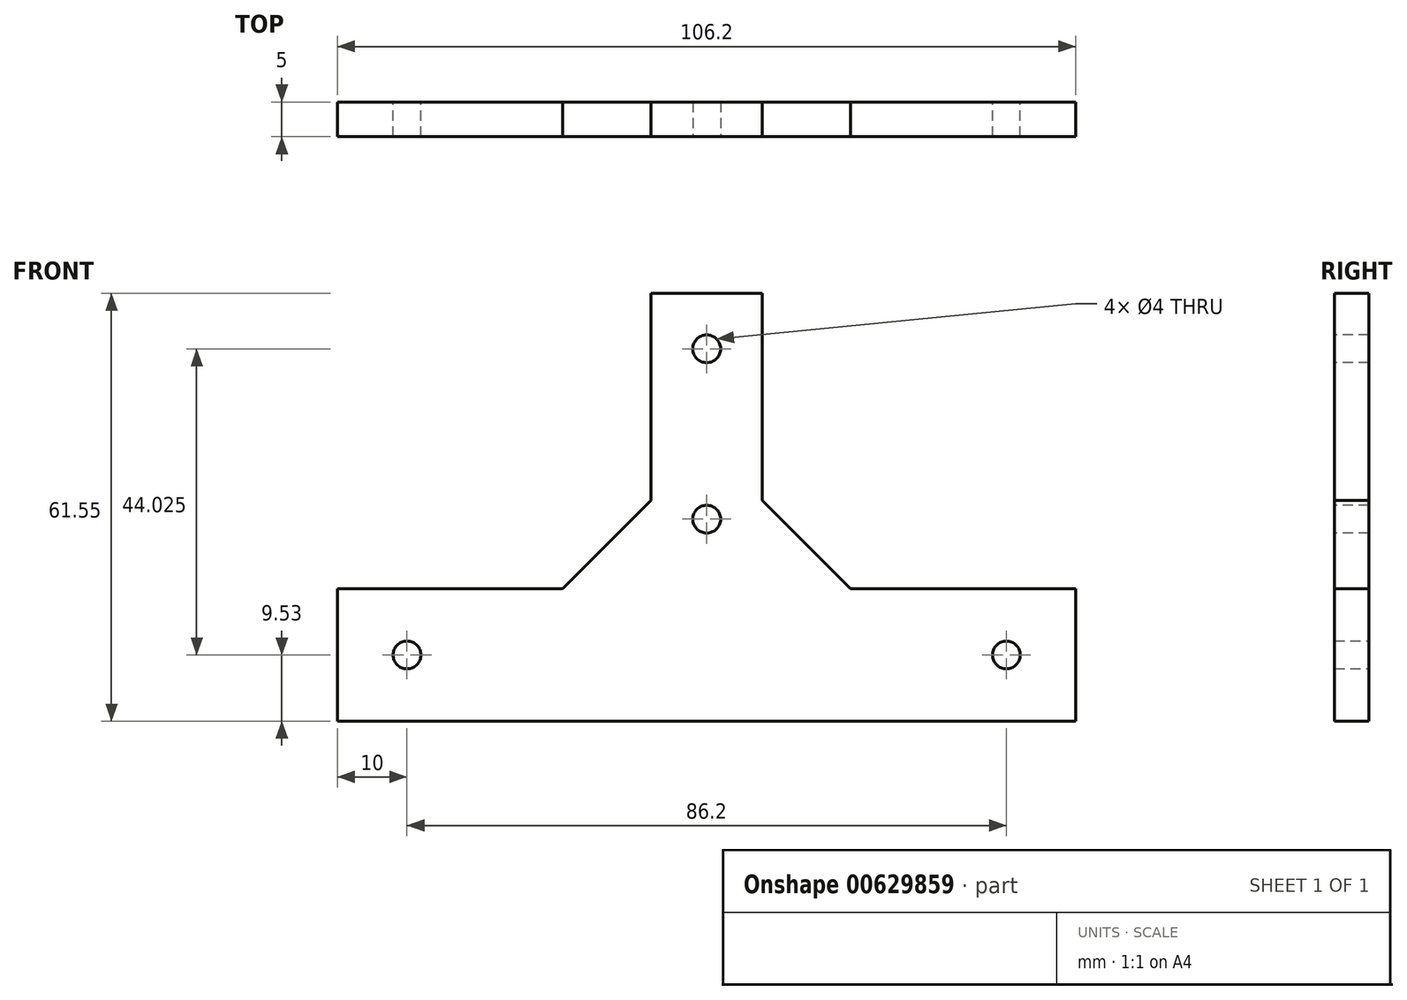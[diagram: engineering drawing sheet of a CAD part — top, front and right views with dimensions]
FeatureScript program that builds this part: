
annotation { "Feature Type Name" : "Feature", "Feature Type Description" : "" }
export const myFeature = defineFeature(function(context is Context, id is Id, definition is map)
    precondition{}
    {
        {
            var Q0;
            Q0=qCreatedBy(makeId("Front.planeOp"),FACE);
            var sketch = newSketch(context, id + "F0", { "sketchPlane" : qUnion([Q0])});
            skLineSegment(sketch, "E0.bottom", {"start": v(53.1, 12.7) * mm, "end": v(-53.1, 12.7) * mm, "construction": true});
            skLineSegment(sketch, "E0.top", {"start": v(53.1, -12.7) * mm, "end": v(-53.1, -12.7) * mm, "construction": true});
            skLineSegment(sketch, "E0.left", {"start": v(53.1, 12.7) * mm, "end": v(53.1, -12.7) * mm, "construction": true});
            skLineSegment(sketch, "E0.right", {"start": v(-53.1, 12.7) * mm, "end": v(-53.1, -12.7) * mm, "construction": true});
            skPoint(sketch, "E0.middle", {"position": v(0, 0) * mm});
            skLineSegment(sketch, "E1.bottom", {"start": v(15, 62.7) * mm, "end": v(-15, 62.7) * mm});
            skLineSegment(sketch, "E1.left", {"start": v(15, 62.7) * mm, "end": v(15, -12.7) * mm});
            skLineSegment(sketch, "E1.right", {"start": v(-15, 62.7) * mm, "end": v(-15, -12.7) * mm});
            skPoint(sketch, "E1.top.end.orphan", {"position": v(-15, -62.7) * mm});
            skPoint(sketch, "E2.orphan", {"position": v(15, -62.7) * mm});
            skLineSegment(sketch, "E3", {"start": v(-53.1, 9.52) * mm, "end": v(53.1, 9.53) * mm});
            skLineSegment(sketch, "E4", {"start": v(53.1, 9.53) * mm, "end": v(53.1, -9.52) * mm});
            skLineSegment(sketch, "E5", {"start": v(53.1, -9.52) * mm, "end": v(-53.1, -9.52) * mm});
            skLineSegment(sketch, "E6", {"start": v(-53.1, -9.53) * mm, "end": v(-53.1, 9.52) * mm});
            skLineSegment(sketch, "E7", {"start": v(-53.1, -9.53) * mm, "end": v(53.1, 9.53) * mm, "construction": true});
            skLineSegment(sketch, "E8", {"start": v(-53.1, 0) * mm, "end": v(53.1, 0) * mm, "construction": true});
            skCircle(sketch, "E9", {"center": v(-43.1, 0) * mm, "radius": 2 * mm});
            skLineSegment(sketch, "E10", {"start": v(0, 9.53) * mm, "end": v(0, -9.52) * mm, "construction": true});
            skCircle(sketch, "E11.MirrorC", {"center": v(43.1, 0) * mm, "radius": 2 * mm});
            skSolve(sketch);
        }
        {
            var Q0;
            {var subQ0=sQuery(id+"F0.wireOp",EDGE,"E0.left");Q0=makeQuery(id+"F0.imprint","IMPRINT",FACE,{"disambiguationData":[TD([[makeQuery(id+"F0.imprint","IMPRINT",EDGE,{"derivedFrom":subQ0}),-1.0]])]});}
            var Q1;
            {var subQ0=sQuery(id+"F0.wireOp",EDGE,"E1.left");var subQ1=sQuery(id+"F0.wireOp",EDGE,"E0.bottom");var subQ2=makeQuery(id+"F0.imprint","INTERSECT",VERTEX,{"derivedFrom":[subQ1,subQ0]});Q1=makeQuery(id+"F0.imprint","IMPRINT",FACE,{"disambiguationData":[TD([[makeQuery(id+"F0.imprint","IMPRINT",EDGE,{"disambiguationData":[TD([[subQ2,-1.0]])],"derivedFrom":subQ1}),1.0]])]});}
            var Q2;
            {var subQ5=sQuery(id+"F0.wireOp",EDGE,"E1.bottom");Q2=makeQuery(id+"F0.imprint","IMPRINT",FACE,{"disambiguationData":[TD([[makeQuery(id+"F0.imprint","IMPRINT",EDGE,{"derivedFrom":subQ5}),1.0]])]});}
            var Q3;
            {var subQ0=sQuery(id+"F0.wireOp",EDGE,"E0.right");Q3=makeQuery(id+"F0.imprint","IMPRINT",FACE,{"disambiguationData":[TD([[makeQuery(id+"F0.imprint","IMPRINT",EDGE,{"derivedFrom":subQ0}),1.0]])]});}
            var Q4;
            {var subQ0=sQuery(id+"F0.wireOp",EDGE,"E6");Q4=makeQuery(id+"F0.imprint","IMPRINT",FACE,{"disambiguationData":[TD([[makeQuery(id+"F0.imprint","IMPRINT",EDGE,{"derivedFrom":subQ0}),-1.0]])]});}
            var Q5;
            {var subQ0=sQuery(id+"F0.wireOp",EDGE,"E5");var subQ1=sQuery(id+"F0.wireOp",EDGE,"E1.left");var subQ2=makeQuery(id+"F0.imprint","INTERSECT",VERTEX,{"derivedFrom":[subQ1,subQ0]});Q5=makeQuery(id+"F0.imprint","IMPRINT",FACE,{"disambiguationData":[TD([[makeQuery(id+"F0.imprint","IMPRINT",EDGE,{"disambiguationData":[TD([[subQ2,1.0]])],"derivedFrom":subQ1}),-1.0]])]});}
            var Q6;
            {var subQ1=sQuery(id+"F0.wireOp",EDGE,"E4");Q6=makeQuery(id+"F0.imprint","IMPRINT",FACE,{"disambiguationData":[TD([[makeQuery(id+"F0.imprint","IMPRINT",EDGE,{"derivedFrom":subQ1}),-1.0]])]});}
            extrude(context, id + "F1", {"entities" : qUnion([Q0, Q1, Q2, Q3, Q4, Q5, Q6]), "depth" : 5 * mm, "offsetDistance" : 25.4 * mm});
        }
        {
            var Q0;
            Q0=makeQuery(id+"F1.opExtrude","SWEPT_EDGE",EDGE,{"disambiguationData":[OSD([sQuery(id+"F0.wireOp",EDGE,"E1.left"),sQuery(id+"F0.wireOp",EDGE,"E3")])]});
            var Q1;
            Q1=makeQuery(id+"F1.opExtrude","SWEPT_EDGE",EDGE,{"disambiguationData":[OSD([sQuery(id+"F0.wireOp",EDGE,"E1.right"),sQuery(id+"F0.wireOp",EDGE,"E3")])]});
            chamfer(context, id + "F2", {"entities" : qUnion([Q0, Q1]), "width" : 19.05 * mm, "tangentPropagation" : true});
        }
        {
            var Q0;
            Q0=makeQuery(id+"F1.opExtrude","CAP_FACE",FACE,{"disambiguationData":[OSD([sQuery(id+"F0.wireOp",EDGE,"E1.bottom"),sQuery(id+"F0.wireOp",EDGE,"E1.left"),sQuery(id+"F0.wireOp",EDGE,"E1.right"),sQuery(id+"F0.wireOp",EDGE,"E3"),sQuery(id+"F0.wireOp",EDGE,"E4"),sQuery(id+"F0.wireOp",EDGE,"E5"),sQuery(id+"F0.wireOp",EDGE,"E6"),sQuery(id+"F0.wireOp",EDGE,"E9"),sQuery(id+"F0.wireOp",EDGE,"E11.MirrorC")])],"isStart":false});
            var sketch = newSketch(context, id + "F3", { "sketchPlane" : qUnion([Q0])});
            skLineSegment(sketch, "E12", {"start": v(0, 62.7) * mm, "end": v(0, 0) * mm, "construction": true});
            skPoint(sketch, "E13.middle", {"position": v(0, 40.68) * mm});
            skCircle(sketch, "E14", {"center": v(0, 44.02) * mm, "radius": 2 * mm});
            skCircle(sketch, "E15", {"center": v(0, 19.53) * mm, "radius": 2 * mm});
            skLineSegment(sketch, "E16", {"start": v(0, 44.02) * mm, "end": v(0, 19.53) * mm});
            skLineSegment(sketch, "E17.bottom", {"start": v(8, 52.02) * mm, "end": v(-8, 52.02) * mm});
            skLineSegment(sketch, "E17.top", {"start": v(8, 11.53) * mm, "end": v(-8, 11.53) * mm});
            skLineSegment(sketch, "E17.left", {"start": v(8, 52.02) * mm, "end": v(8, 11.53) * mm});
            skLineSegment(sketch, "E17.right", {"start": v(-8, 52.02) * mm, "end": v(-8, 11.53) * mm});
            skPoint(sketch, "E17.middle", {"position": v(0, 31.77) * mm});
            skLineSegment(sketch, "E18", {"start": v(-34.05, 9.52) * mm, "end": v(34.05, 9.53) * mm});
            skLineSegment(sketch, "E19", {"start": v(-8, 11.53) * mm, "end": v(-8, 9.53) * mm});
            skLineSegment(sketch, "E20", {"start": v(8, 11.53) * mm, "end": v(8, 9.53) * mm});
            skSolve(sketch);
        }
        {
            var Q0;
            Q0=makeQuery(id+"F3.imprint","IMPRINT",FACE,{"disambiguationData":[TD([[makeQuery(id+"F3.imprint","IMPRINT",EDGE,{"derivedFrom":sQuery(id+"F3.wireOp",EDGE,"E17.bottom")}),-1.0]])]});
            extrude(context, id + "F4", {"entities" : qUnion([Q0]), "operationType" : NewBodyOperationType.REMOVE, "endBound" : BoundingType.THROUGH_ALL, "oppositeDirection" : true, "depth" : 25.4 * mm, "offsetDistance" : 25.4 * mm});
        }
        {
            var Q0;
            Q0=makeQuery(id+"F3.imprint","IMPRINT",FACE,{"disambiguationData":[TD([[makeQuery(id+"F3.imprint","IMPRINT",EDGE,{"derivedFrom":sQuery(id+"F3.wireOp",EDGE,"E14")}),1.0]])]});
            var Q1;
            Q1=makeQuery(id+"F3.imprint","IMPRINT",FACE,{"disambiguationData":[TD([[makeQuery(id+"F3.imprint","IMPRINT",EDGE,{"derivedFrom":sQuery(id+"F3.wireOp",EDGE,"E15")}),1.0]])]});
            extrude(context, id + "F5", {"entities" : qUnion([Q0, Q1]), "operationType" : NewBodyOperationType.REMOVE, "oppositeDirection" : true, "depth" : 25.4 * mm, "offsetDistance" : 25.4 * mm});
        }
        {
            var Q0;
            Q0=makeQuery(id+"F4.boolean.opBoolean","COPY",EDGE,{"derivedFrom":makeQuery(id+"F4.opExtrude","SWEPT_EDGE",EDGE,{"disambiguationData":[OSD([sQuery(id+"F3.wireOp",EDGE,"E18"),sQuery(id+"F3.wireOp",EDGE,"E20")])]})});
            var Q1;
            Q1=makeQuery(id+"F4.boolean.opBoolean","COPY",EDGE,{"derivedFrom":makeQuery(id+"F4.opExtrude","SWEPT_EDGE",EDGE,{"disambiguationData":[OSD([sQuery(id+"F3.wireOp",EDGE,"E18"),sQuery(id+"F3.wireOp",EDGE,"E19")])]})});
            chamfer(context, id + "F6", {"entities" : qUnion([Q0, Q1]), "width" : 12.7 * mm, "tangentPropagation" : true});
        }
    });
